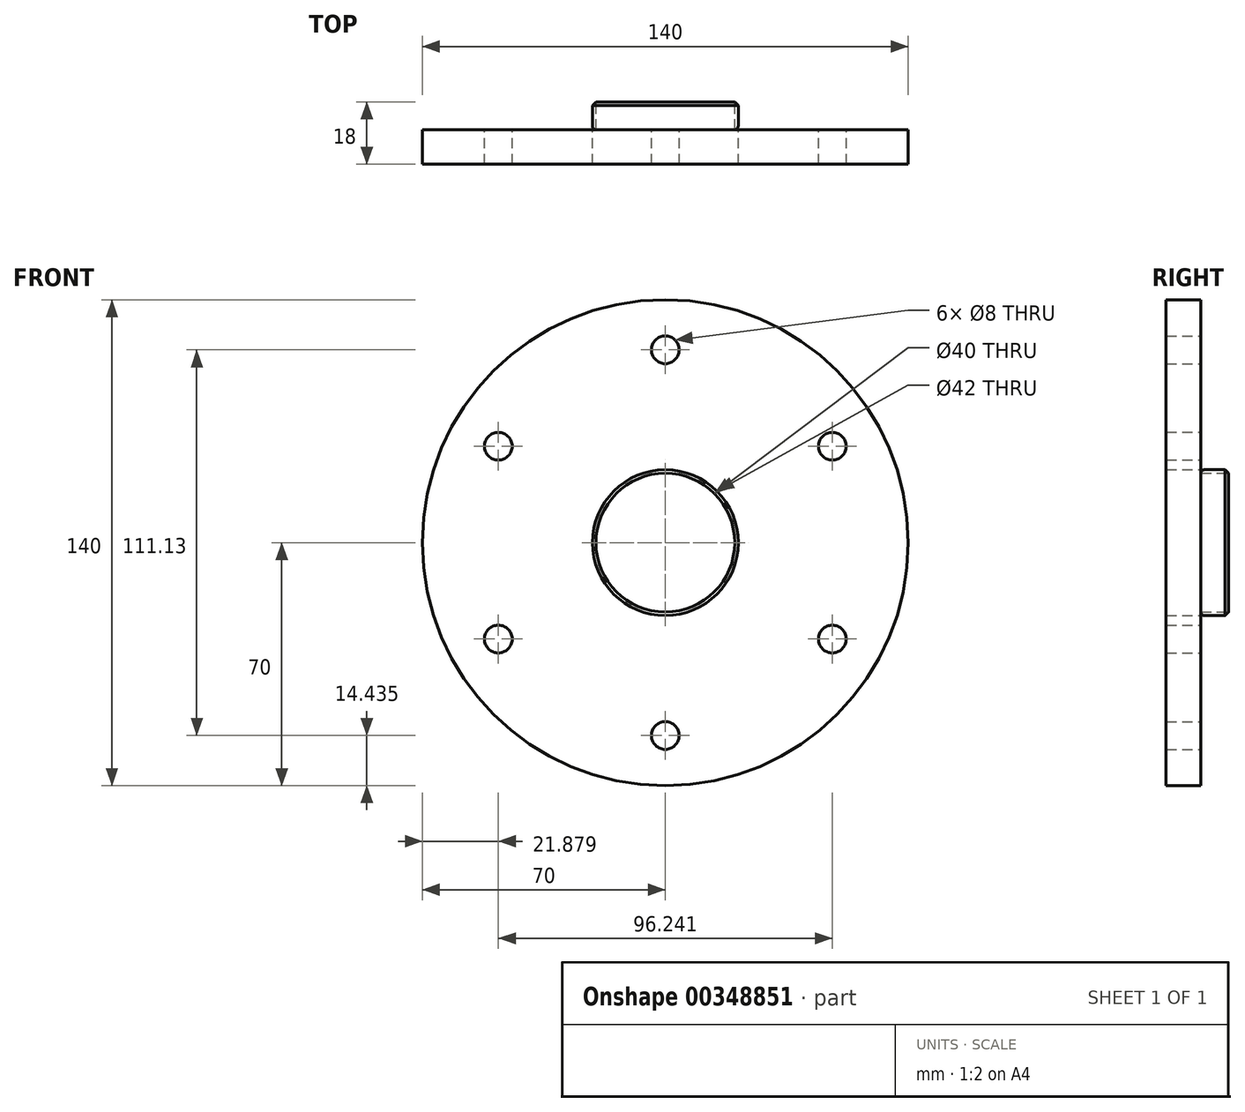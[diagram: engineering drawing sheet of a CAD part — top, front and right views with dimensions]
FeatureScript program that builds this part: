
annotation { "Feature Type Name" : "Feature", "Feature Type Description" : "" }
export const myFeature = defineFeature(function(context is Context, id is Id, definition is map)
    precondition{}
    {
        {
            var Q0;
            Q0=qCreatedBy(makeId("Front.planeOp"),FACE);
            var sketch = newSketch(context, id + "F0", { "sketchPlane" : qUnion([Q0])});
            skCircle(sketch, "E0", {"center": v(0, 0) * mm, "radius": 55.56 * mm, "construction": true});
            skCircle(sketch, "E1", {"center": v(0, 0) * mm, "radius": 70 * mm});
            skCircle(sketch, "E2", {"center": v(0, 55.56) * mm, "radius": 4 * mm});
            skCircle(sketch, "E3.1.0", {"center": v(-48.12, 27.78) * mm, "radius": 4 * mm});
            skCircle(sketch, "E3.2.0", {"center": v(-48.12, -27.78) * mm, "radius": 4 * mm});
            skCircle(sketch, "E3.3.0", {"center": v(0, -55.56) * mm, "radius": 4 * mm});
            skCircle(sketch, "E3.4.0", {"center": v(48.12, -27.78) * mm, "radius": 4 * mm});
            skCircle(sketch, "E3.5.0", {"center": v(48.12, 27.78) * mm, "radius": 4 * mm});
            skLineSegment(sketch, "E4", {"start": v(0, 0) * mm, "end": v(48.12, 27.78) * mm, "construction": true});
            skLineSegment(sketch, "E5", {"start": v(0, 0) * mm, "end": v(48.12, -27.78) * mm, "construction": true});
            skLineSegment(sketch, "E6", {"start": v(0, 93.04) * mm, "end": v(0, -80.3) * mm, "construction": true});
            skLineSegment(sketch, "E7", {"start": v(0, 0) * mm, "end": v(-48.12, 27.78) * mm, "construction": true});
            skLineSegment(sketch, "E8", {"start": v(0, 0) * mm, "end": v(-48.12, -27.78) * mm, "construction": true});
            skLineSegment(sketch, "E9", {"start": v(0, 0) * mm, "end": v(0, -55.56) * mm, "construction": true});
            skCircle(sketch, "E10", {"center": v(0, 0) * mm, "radius": 21 * mm});
            skSolve(sketch);
        }
        {
            var Q0;
            Q0=makeQuery(id+"F0.imprint","IMPRINT",FACE,{"disambiguationData":[TD([[makeQuery(id+"F0.imprint","IMPRINT",EDGE,{"derivedFrom":sQuery(id+"F0.wireOp",EDGE,"E1")}),1.0]])]});
            extrude(context, id + "F1", {"entities" : qUnion([Q0]), "depth" : 10 * mm});
        }
        {
            var Q0;
            Q0=qCreatedBy(makeId("Front.planeOp"),FACE);
            var sketch = newSketch(context, id + "F2", { "sketchPlane" : qUnion([Q0])});
            skCircle(sketch, "E11", {"center": v(0, 0) * mm, "radius": 21 * mm});
            skSolve(sketch);
        }
        {
            var Q0;
            Q0=makeQuery(id+"F2.imprint","IMPRINT",FACE,{"disambiguationData":[TD([[makeQuery(id+"F2.imprint","IMPRINT",EDGE,{"derivedFrom":sQuery(id+"F2.wireOp",EDGE,"E11")}),1.0]])]});
            extrude(context, id + "F3", {"entities" : qUnion([Q0]), "operationType" : NewBodyOperationType.ADD, "oppositeDirection" : true, "depth" : 8 * mm});
        }
        {
            var Q0;
            Q0=makeQuery(id+"F3.opExtrude","CAP_EDGE",EDGE,{"disambiguationData":[OSD([sQuery(id+"F2.wireOp",EDGE,"E11")])],"isStart":false});
            chamfer(context, id + "F4", {"entities" : qUnion([Q0]), "width" : 1 * mm, "tangentPropagation" : true});
        }
        {
            var Q0;
            Q0=makeQuery(id+"F3.opExtrude","CAP_EDGE",EDGE,{"disambiguationData":[OSD([sQuery(id+"F2.wireOp",EDGE,"E11")])],"isStart":true});
            fillet(context, id + "F5", {"entities" : qUnion([Q0]), "radius" : 1 * mm, "tangentPropagation" : true, "allowEdgeOverflow" : false});
        }
        {
            var Q0;
            Q0=makeQuery(id+"F3.opExtrude","CAP_FACE",FACE,{"disambiguationData":[OSD([sQuery(id+"F2.wireOp",EDGE,"E11")])],"isStart":false});
            var sketch = newSketch(context, id + "F6", { "sketchPlane" : qUnion([Q0])});
            skCircle(sketch, "E12", {"center": v(0, 0) * mm, "radius": 21 * mm});
            skSolve(sketch);
        }
        {
            var Q0;
            {var subQ0=sQuery(id+"F2.wireOp",EDGE,"E11");Q0=makeQuery(id+"F6.imprint","IMPRINT",FACE,{"disambiguationData":[TD([[makeQuery(id+"F6.imprint","IMPRINT",EDGE,{"derivedFrom":makeQuery(id+"F4.opChamfer","BLEND_EDGE",EDGE,{"blendedFrom":[makeQuery(id+"F3.opExtrude","CAP_EDGE",EDGE,{"disambiguationData":[OSD([subQ0])],"isStart":false}),makeQuery(id+"F3.opExtrude","CAP_FACE",FACE,{"disambiguationData":[OSD([subQ0])],"isStart":false})],"blendedInto":[makeQuery(id+"F3.opExtrude","CAP_FACE",FACE,{"disambiguationData":[OSD([subQ0])],"isStart":false})]})}),1.0]])]});}
            extrude(context, id + "F7", {"entities" : qUnion([Q0]), "operationType" : NewBodyOperationType.REMOVE, "oppositeDirection" : true, "depth" : 20 * mm});
        }
    });
